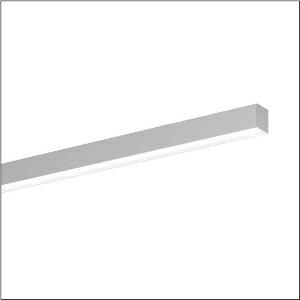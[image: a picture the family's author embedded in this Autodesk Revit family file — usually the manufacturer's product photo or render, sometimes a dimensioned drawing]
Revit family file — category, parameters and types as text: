
# Revit family: silica_r__21_51mx23da44sb_489f
name_source: partatom
category: Lighting Fixtures
units: mm (PartAtom-declared; Revit-internal decimal feet)

## family parameters
Cut with Voids When Loaded = No
Host = Face
Light Source = No
Part Type = Normal
Room Calculation Point = No
Round Connector Dimension = Use Diameter
Shared = No

## types (1)
- --- (1 x LED, 3280 lm, 22.4 W, 4000K)
    Apparent Load = 22 VA
    CIE Flux Codes = 78 96 99 100 100
    Color Rendering = 80
    Color Temperature = 4000K
    Default Elevation = 1800 mm
    Description = Silica® 21, office luminaire, primary optical cover: prismatic diffuser, of PMMA, CAT 2 (L<= 3000cd/m²), light emission: direct distribution, primary light characteristic: symmetric, installation type: surface-mounted, LED, rated luminous flux: 3.280lm, luminous efficacy: 146lm/W, light colour: 840, colour temperature: 4000K, with terminal, 3+2-pole, max. 2.5mm², mains connection: 220..240V, AC, 50/60Hz, rated input power: 22.4W, luminaire housing, of aluminium, metallic grey (RAL 9006), length: 1.204mm, width: 53mm, height: 53mm, protection rating (complete): IP20, insulation class (complete): insulation class I (protective earthing), certification: CE, permissible operating ambient temperature: 0..+35°C, standard: EN 50419, packaging unit: 1 piece
    Height = 0 mm  [stored 0 ft]
    Lamp = 1 x LED
    Lamp Light Flux = 3280 lm
    Lamp Power = 22.4 W
    Lamp count = 1
    Length = 1204 mm
    Luminous efficacy = 146 lm/W
    Manufacturer = Siteco
    ModVariant = No
    Model = 51MX23DA44SB
    Mounting Place = Ceiling
    Mounting Type = Recessed
    Number of Poles = 1
    OnlyDefault = Yes
    Power Factor = 1
    Product Name = Silica® 21
    Product group = office luminaire | ceiling recessed
    ProductGroupID = 401
    Protection Class = Protection class I
    Protection Degree = IP 20
    RLX_Detail_Level = 1
    RLX_Emergency_Light_Flux = 0 lm
    RLX_Emergency_Type = 0
    RLX_Emergency_Type_DB = No
    RlxData = <blob elided: 21225 chars, md5=3b46707c>
    Socket = socket
    Standby Power = 0 W
    System Light Flux = 3280 lm
    System Power = 22 W
    Type Comments = factory setting: luminous flux: 100 % | dim-lin: 254 | 323 mA
    Type Image = l_1313588.jpg
    URL = http://relux.com
    VarID = @adj_067939
    Voltage = 0 V
    Weight = 0.00 kg
    Width = 53 mm

note: [stored X ft] marks values corroborated as IEEE doubles in the binary element streams (Revit-internal decimal feet)

## geometry (parser evidence)
native form markers: Blend x4, Sweep x11
no freeform markers — native parametric forms only
